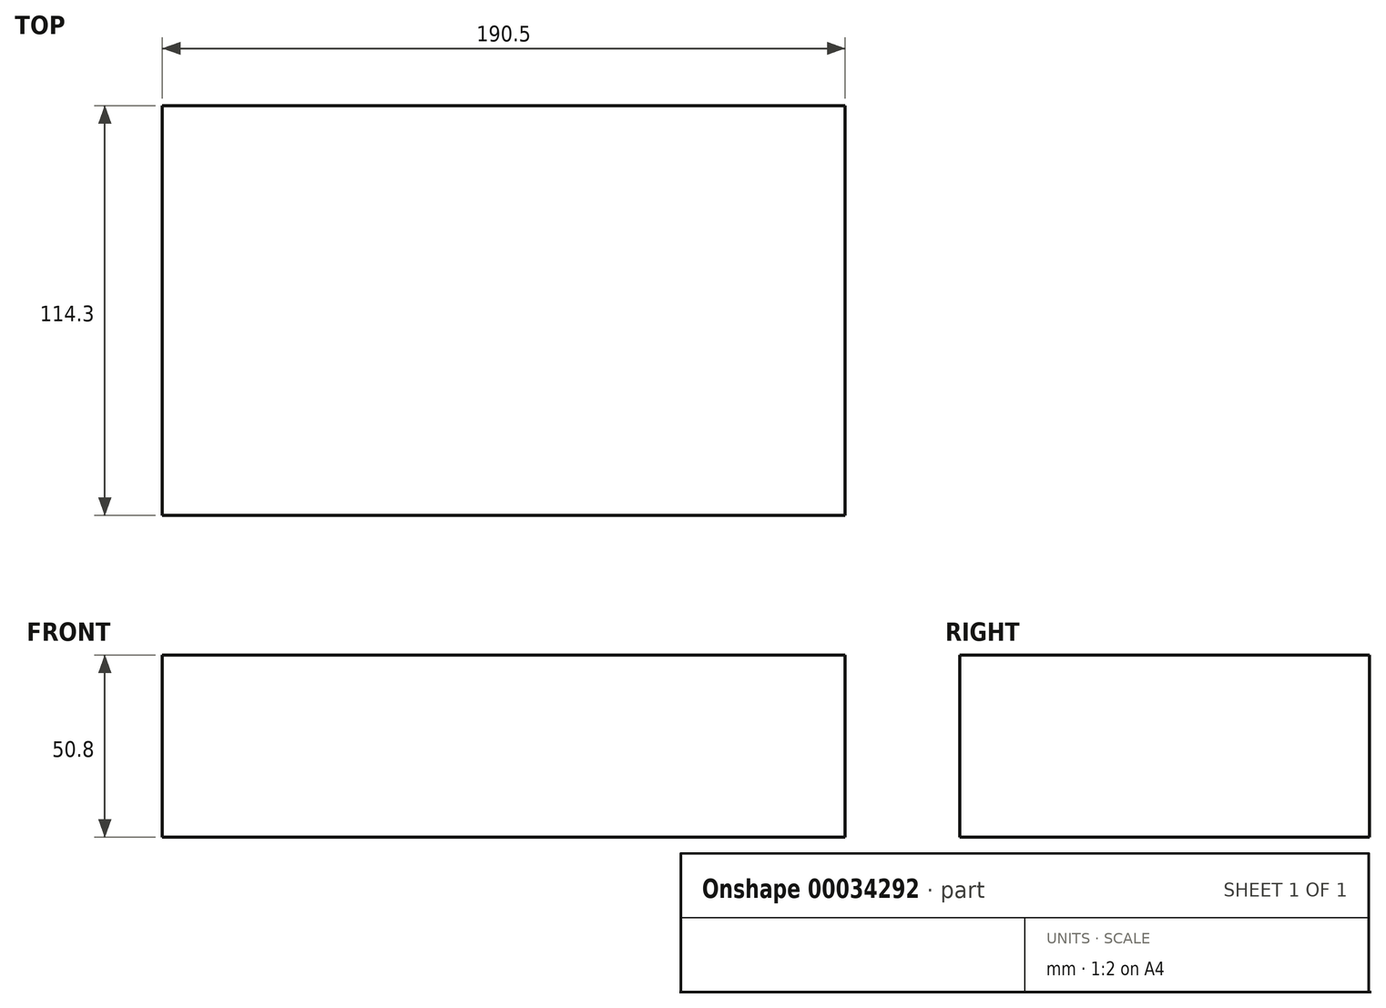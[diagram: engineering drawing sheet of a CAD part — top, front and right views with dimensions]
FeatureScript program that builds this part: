
annotation { "Feature Type Name" : "Feature", "Feature Type Description" : "" }
export const myFeature = defineFeature(function(context is Context, id is Id, definition is map)
    precondition{}
    {
        {
            var Q0;
            Q0=qCreatedBy(makeId("Top.planeOp"),FACE);
            var sketch = newSketch(context, id + "F0", { "sketchPlane" : qUnion([Q0])});
            skLineSegment(sketch, "E0.bottom", {"start": v(-212.01, -54.2) * mm, "end": v(-21.51, -54.2) * mm});
            skLineSegment(sketch, "E0.top", {"start": v(-212.01, 60.1) * mm, "end": v(-21.51, 60.1) * mm});
            skLineSegment(sketch, "E0.left", {"start": v(-212.01, -54.2) * mm, "end": v(-212.01, 60.1) * mm});
            skLineSegment(sketch, "E0.right", {"start": v(-21.51, -54.2) * mm, "end": v(-21.51, 60.1) * mm});
            skSolve(sketch);
        }
        {
            var Q0;
            Q0 = qSketchRegion(id + "F0", true);
            extrude(context, id + "F1", {"entities" : qUnion([Q0]), "depth" : 50.8 * mm});
        }
    });
